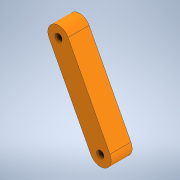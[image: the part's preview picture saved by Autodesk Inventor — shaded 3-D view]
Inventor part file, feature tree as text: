
AUTODESK INVENTOR PART (.ipt)
format: ipt  version: 2021 (Build 250183000, 183)  size: 109,056 bytes
history: native  units: mm
features: extrude x1, sketch x1
ambient origin geometry x8: Origin, YZ Plane, XZ Plane, XY Plane, X Axis, Y Axis, Z Axis, Center Point
bodies: Solid1 (feature_tree)
feature tree (2):
  extrude  "Extrusion1"  Depth=147.0mm
  sketch  "Sketch1"  dims[d0=150.0mm d1=50.0mm d2=150.0mm d3=50.0mm d4=562.0mm d5=147.0mm d6=0.0mm d7=0.5mm d8=0.872665mm]
